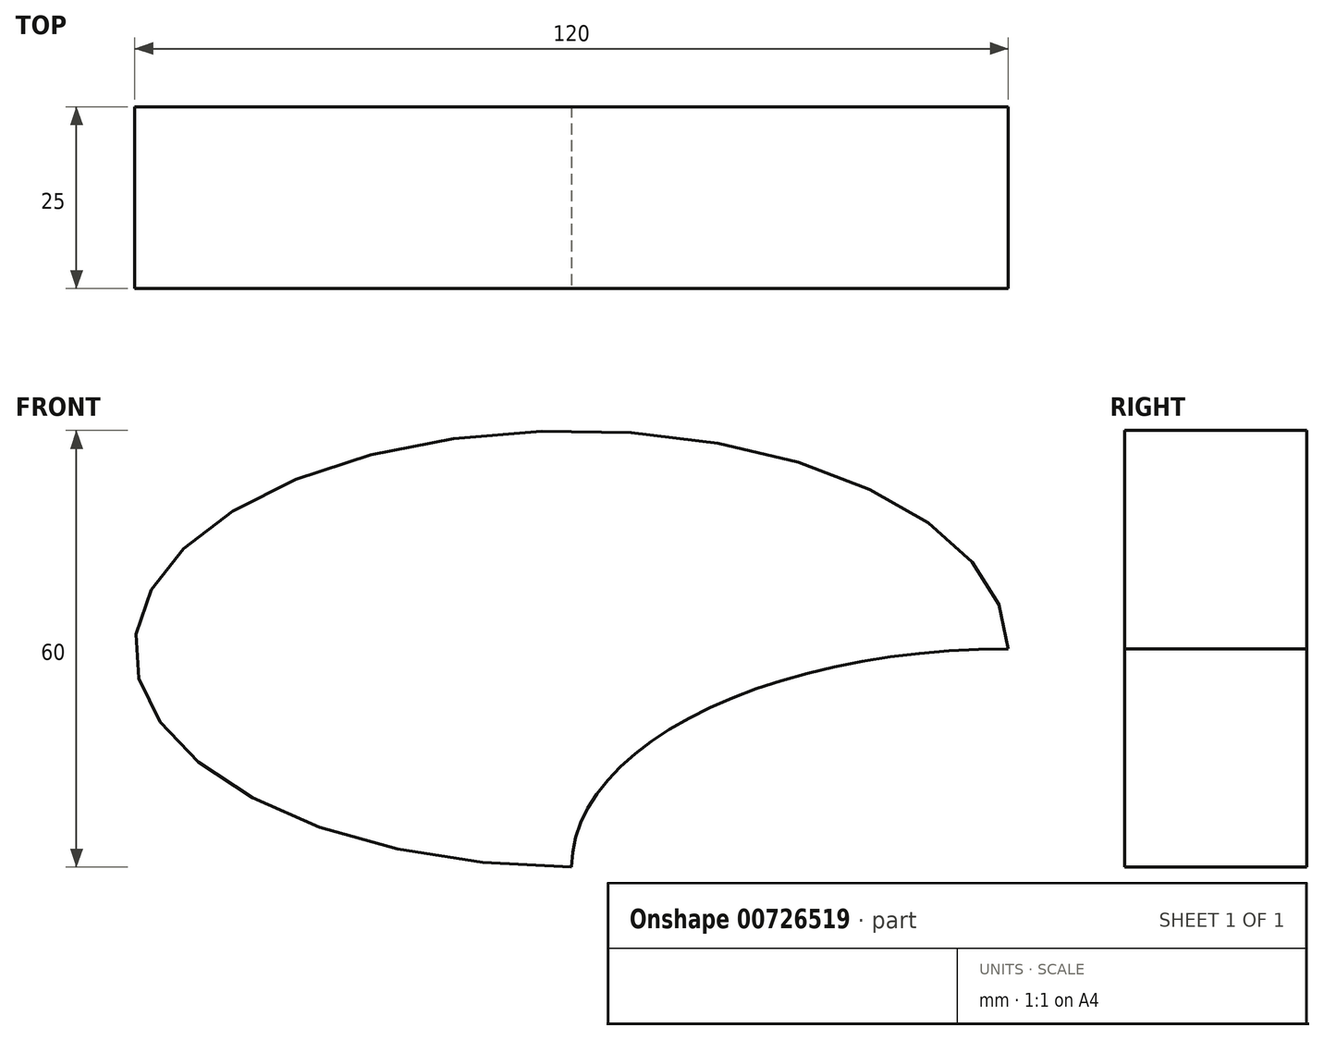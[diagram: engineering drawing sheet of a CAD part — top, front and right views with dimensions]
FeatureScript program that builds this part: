
annotation { "Feature Type Name" : "Feature", "Feature Type Description" : "" }
export const myFeature = defineFeature(function(context is Context, id is Id, definition is map)
    precondition{}
    {
        {
            var Q0;
            Q0=qCreatedBy(makeId("Front.planeOp"),FACE);
            var sketch = newSketch(context, id + "F0", { "sketchPlane" : qUnion([Q0])});
            skEllipticalArc(sketch, "E0", {});
            skEllipticalArc(sketch, "E1", {});
            const initialGuessF0  = {"E0": [0.06, 0, 1, 0, 0.06, 0.03, 0, 4.71238898038469], "E1": [0.12, -0.03, 1, 0, 0.06, 0.03, 1.5707963267948966, 3.141592653589793]};
            skSetInitialGuess(sketch, initialGuessF0);
            skSolve(sketch);
        }
        {
            var Q0;
            Q0 = qSketchRegion(id + "F0", true);
            extrude(context, id + "F1", {"entities" : qUnion([Q0]), "oppositeDirection" : true, "depth" : 25 * mm, "offsetDistance" : 25 * mm});
        }
    });
